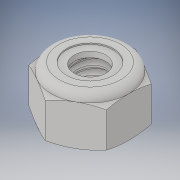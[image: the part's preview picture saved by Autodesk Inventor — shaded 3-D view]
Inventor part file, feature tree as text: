
AUTODESK INVENTOR PART (.ipt)
format: ipt  version: 2018 (Build 220112000, 112)  size: 291,328 bytes
history: native  units: in
note: dims shown in document units (in); Inventor stores cm internally (conversion verified against a paired STEP export)
features: other x1, revolve x1
ambient origin geometry x8: Origin, YZ Plane, XZ Plane, XY Plane, X Axis, Y Axis, Z Axis, Center Point
bodies: Solid1 (feature_tree), Solid2 (feature_tree)
feature tree (2):
  other  "Cut-Revolve4"
  revolve  "Revolve2"  [1 undecoded]
note: 1 required parameter value undecoded (feature->parameter linkage not recoverable at this tier; creation-order binding heuristic only, values carry confidence <= 0.55)
